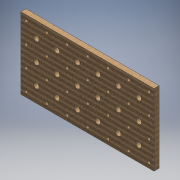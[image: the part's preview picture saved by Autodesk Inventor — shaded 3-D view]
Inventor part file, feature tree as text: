
AUTODESK INVENTOR PART (.ipt)
format: ipt  version: 2016 (Build 200138000, 138)  size: 213,504 bytes
history: native  units: mm
features: extrude x1, sketch x1
ambient origin geometry x8: Origin, YZ Plane, XZ Plane, XY Plane, X Axis, Y Axis, Z Axis, Center Point
bodies: Body1 (feature_tree)
feature tree (2):
  extrude  "Extrusion3"  Depth=5.95mm
  sketch  "Sketch1"  dims[d0=18.0mm d1=2.0mm d2=3.43mm d6=6.35mm d25=40.0mm d27=360.0deg d29=45.0deg d30=12.0mm d31=30.0mm d33=24.0mm d34=10.0mm d36=10.0mm d38=60.0mm d40=24.0mm d41=10.0mm d43=10.0mm d45=6.0mm d46=6.0mm d47=6.0mm d48=6.0mm d49=5.95mm d50=0.0mm]
